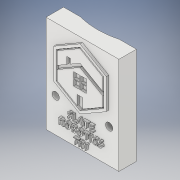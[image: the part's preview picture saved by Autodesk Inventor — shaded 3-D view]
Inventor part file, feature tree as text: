
AUTODESK INVENTOR PART (.ipt)
format: ipt  version: 2017 SP1 (Build 210196100, 196)  size: 1,072,128 bytes
history: native  units: in
note: dims shown in document units (in); Inventor stores cm internally (conversion verified against a paired STEP export)
features: projected_geometry x20, extrude x5, sketch x5, other x3
ambient origin geometry x8: Origin, YZ Plane, XZ Plane, XY Plane, X Axis, Y Axis, Z Axis, Center Point
bodies: Solid2 (feature_tree)
feature tree (33):
  other  "BP002b.ipt"
  extrude  "Extrusion3"  Depth=0.2638in TaperAngle=0.0deg
  extrude  "Extrusion4"  Depth=0.6299in
  extrude  "Extrusion5"  Depth=0.2638in TaperAngle=0.0deg
  extrude  "Extrusion7"  Depth=0.1181in
  extrude  "Extrusion8"  Depth=0.8661in
  other  "Solid1::BP002b.ipt"
  other  "TaggingFeature1"
  sketch  "Sketch4"  dims[d62=0.0394in d63=0.2638in d64=0.0in]
  projected_geometry  "Projected Loop1"
  sketch  "Sketch5"  dims[d65=0.2835in d66=0.0in d67=0.6299in]
  sketch  "Sketch6"  dims[d68=1.2169in d69=0.2638in d70=0.0in]
  sketch  "Sketch9"  dims[d74=0.0315in d75=0.0in d76=0.1181in]
  projected_geometry  "Projected Loop5"
  projected_geometry  "Projected Loop6"
  projected_geometry  "Projected Loop7"
  projected_geometry  "Projected Loop8"
  projected_geometry  "Projected Loop9"
  projected_geometry  "Projected Loop10"
  projected_geometry  "Projected Loop11"
  projected_geometry  "Projected Loop12"
  projected_geometry  "Projected Loop13"
  projected_geometry  "Projected Loop14"
  projected_geometry  "Projected Loop15"
  projected_geometry  "Projected Loop16"
  projected_geometry  "Projected Loop17"
  projected_geometry  "Projected Loop18"
  projected_geometry  "Projected Loop19"
  projected_geometry  "Projected Loop20"
  projected_geometry  "Projected Loop21"
  projected_geometry  "Projected Loop22"
  projected_geometry  "Projected Loop23"
  sketch  "Sketch10"  dims[d77=0.1181in d78=0.8661in d79=1.0236in d80=0.0315in d81=0.0in]
